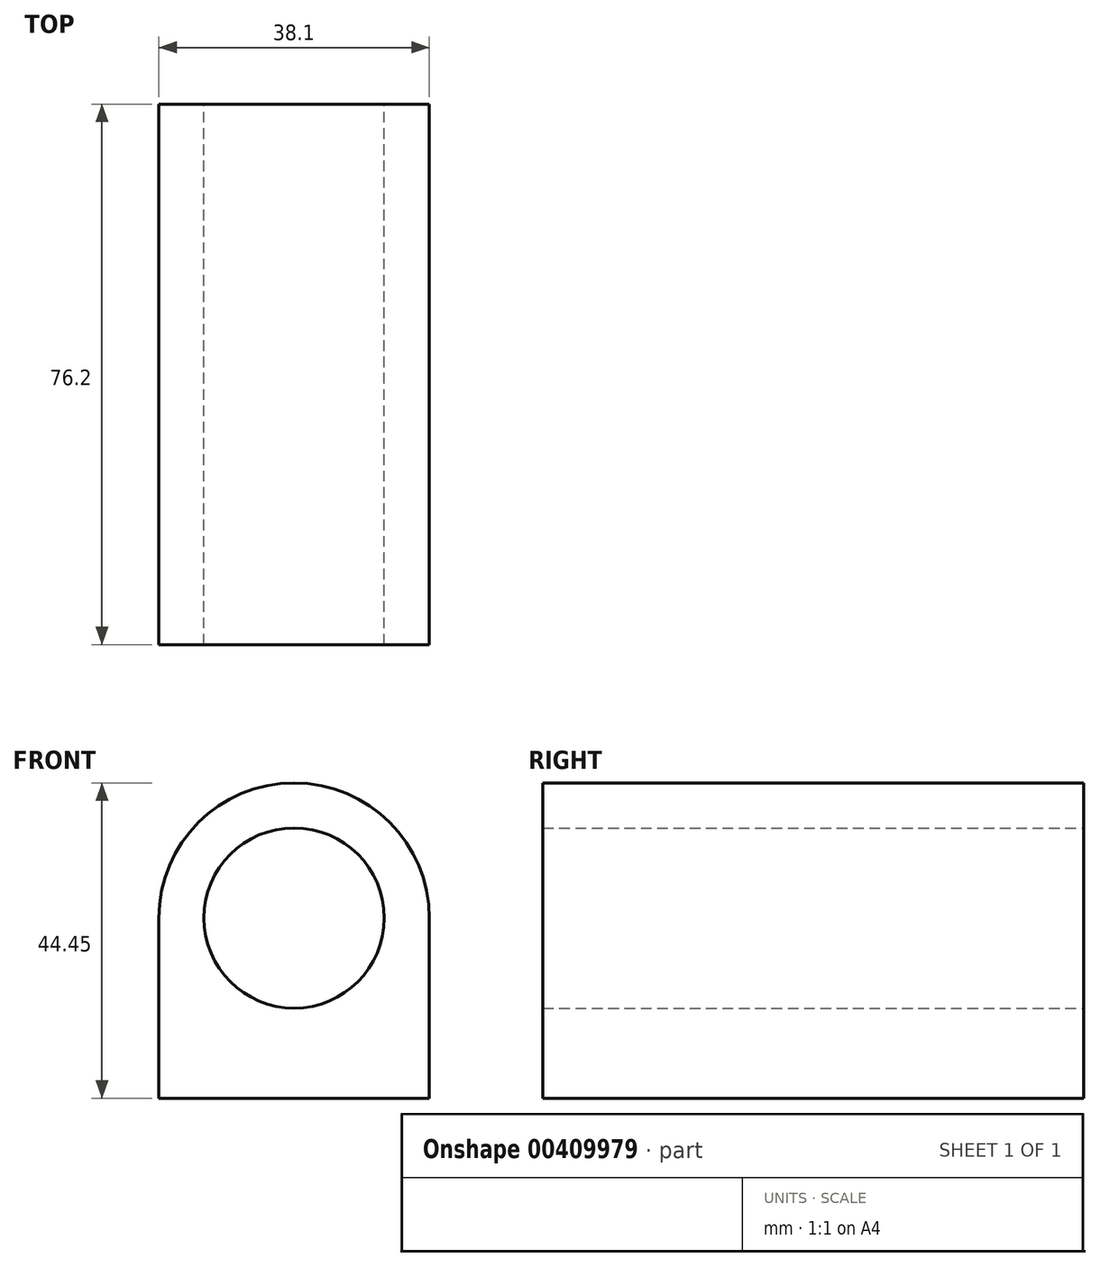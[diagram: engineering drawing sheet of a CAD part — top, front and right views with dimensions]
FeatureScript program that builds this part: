
annotation { "Feature Type Name" : "Feature", "Feature Type Description" : "" }
export const myFeature = defineFeature(function(context is Context, id is Id, definition is map)
    precondition{}
    {
        {
            var Q0;
            Q0=qCreatedBy(makeId("Front.planeOp"),FACE);
            var sketch = newSketch(context, id + "F0", { "sketchPlane" : qUnion([Q0])});
            skCircle(sketch, "E0", {"center": v(0, 0) * mm, "radius": 12.7 * mm});
            skArc(sketch, "E1", {"start": v(19.05, 0) * mm, "mid": v(0, 19.05) * mm, "end": v(-19.05, 0) * mm});
            skLineSegment(sketch, "E2", {"start": v(-19.05, 0) * mm, "end": v(-19.05, -25.4) * mm});
            skLineSegment(sketch, "E3", {"start": v(-19.05, -25.4) * mm, "end": v(19.05, -25.4) * mm});
            skLineSegment(sketch, "E4", {"start": v(19.05, -25.4) * mm, "end": v(19.05, 0) * mm});
            skSolve(sketch);
        }
        {
            var Q0;
            Q0=makeQuery(id+"F0.imprint","IMPRINT",FACE,{"disambiguationData":[TD([[makeQuery(id+"F0.imprint","IMPRINT",EDGE,{"derivedFrom":sQuery(id+"F0.wireOp",EDGE,"E0")}),-1.0]])]});
            extrude(context, id + "F1", {"entities" : qUnion([Q0]), "depth" : 76.2 * mm});
        }
    });
